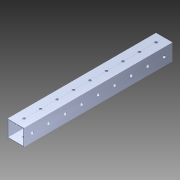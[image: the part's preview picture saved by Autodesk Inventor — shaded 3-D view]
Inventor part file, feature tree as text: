
AUTODESK INVENTOR PART (.ipt)
format: ipt  version: 2014 SP1 (Build 180222100, 222)  size: 1,113,088 bytes
history: native  units: in
note: dims shown in document units (in); Inventor stores cm internally (conversion verified against a paired STEP export)
features: pattern_circular x1, other x1, extrude x1, imported_body x1, sketch x1
ambient origin geometry x8: Origin, YZ Plane, XZ Plane, XY Plane, X Axis, Y Axis, Z Axis, Center Point
bodies: Body1 (feature_tree)
feature tree (5):
  pattern_circular  "CirPattern2"
  other  "1x1 tube1"
  extrude  "Extrusion1"  [1 undecoded]
  imported_body  "Base1"
  sketch  "Sketch1"  dims[d0=50.0in d1=0.0in]
note: 1 required parameter value undecoded (feature->parameter linkage not recoverable at this tier; creation-order binding heuristic only, values carry confidence <= 0.55)
